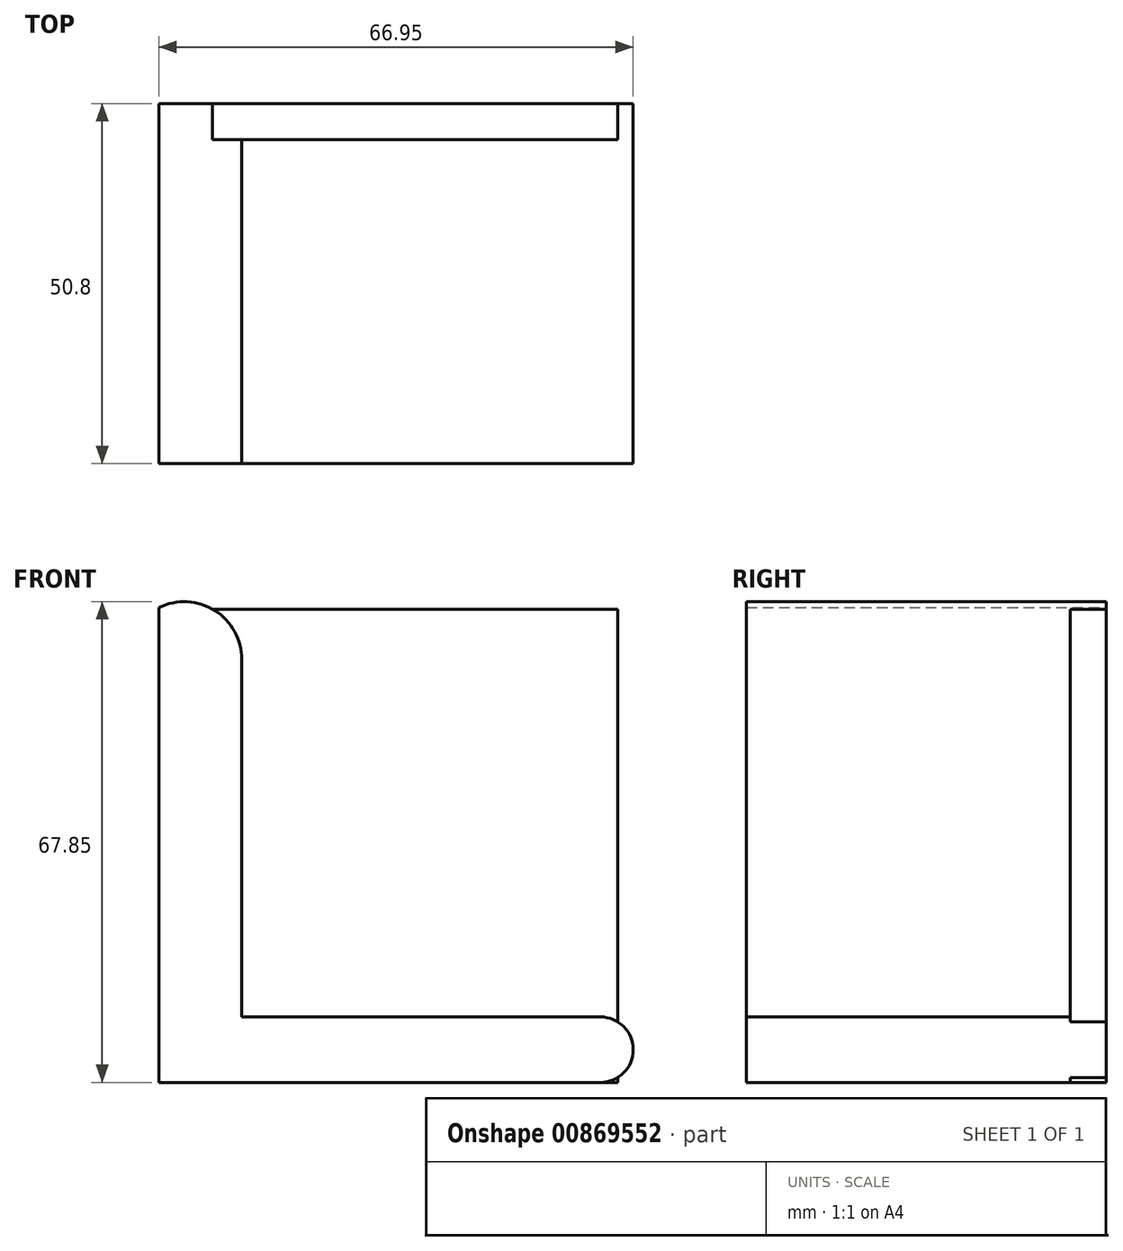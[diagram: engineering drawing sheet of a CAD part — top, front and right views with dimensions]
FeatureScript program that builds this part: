
annotation { "Feature Type Name" : "Feature", "Feature Type Description" : "" }
export const myFeature = defineFeature(function(context is Context, id is Id, definition is map)
    precondition{}
    {
        {
            var Q0;
            Q0=qCreatedBy(makeId("Front.planeOp"),FACE);
            var sketch = newSketch(context, id + "F0", { "sketchPlane" : qUnion([Q0])});
            skLineSegment(sketch, "E0", {"start": v(-51.54, 40.64) * mm, "end": v(-51.54, -26.4) * mm});
            skLineSegment(sketch, "E1", {"start": v(-51.54, -26.4) * mm, "end": v(-39.83, -26.4) * mm});
            skLineSegment(sketch, "E2", {"start": v(-39.83, -26.4) * mm, "end": v(-39.83, 33.29) * mm});
            skArc(sketch, "E3", {"start": v(-39.83, 33.29) * mm, "mid": v(-43.66, 40.2) * mm, "end": v(-51.54, 40.64) * mm});
            skLineSegment(sketch, "E4", {"start": v(-39.83, -26.4) * mm, "end": v(10.79, -26.4) * mm});
            skLineSegment(sketch, "E5", {"start": v(-39.83, -17.16) * mm, "end": v(10.79, -17.16) * mm});
            skArc(sketch, "E6", {"start": v(10.79, -26.4) * mm, "mid": v(15.4, -21.78) * mm, "end": v(10.79, -17.16) * mm});
            skSolve(sketch);
        }
        {
            var Q0;
            Q0 = qSketchRegion(id + "F0", true);
            extrude(context, id + "F1", {"entities" : qUnion([Q0]), "depth" : 50.8 * mm, "offsetDistance" : 25.4 * mm});
        }
        {
            var Q0;
            Q0=qCreatedBy(makeId("Front.planeOp"),FACE);
            var sketch = newSketch(context, id + "F2", { "sketchPlane" : qUnion([Q0])});
            skLineSegment(sketch, "E7.bottom", {"start": v(-51.31, 40.4) * mm, "end": v(13.2, 40.4) * mm});
            skLineSegment(sketch, "E7.top", {"start": v(-51.31, -26.4) * mm, "end": v(13.2, -26.4) * mm});
            skLineSegment(sketch, "E7.left", {"start": v(-51.31, 40.4) * mm, "end": v(-51.31, -26.4) * mm});
            skLineSegment(sketch, "E7.right", {"start": v(13.2, 40.4) * mm, "end": v(13.2, -26.4) * mm});
            skSolve(sketch);
        }
        {
            var Q0;
            Q0=makeQuery(id+"F2.imprint","IMPRINT",FACE,{"disambiguationData":[TD([[makeQuery(id+"F2.imprint","IMPRINT",EDGE,{"derivedFrom":sQuery(id+"F2.wireOp",EDGE,"E7.bottom")}),-1.0]])]});
            extrude(context, id + "F3", {"entities" : qUnion([Q0]), "operationType" : NewBodyOperationType.ADD, "depth" : 5.08 * mm, "offsetDistance" : 25.4 * mm});
        }
    });
